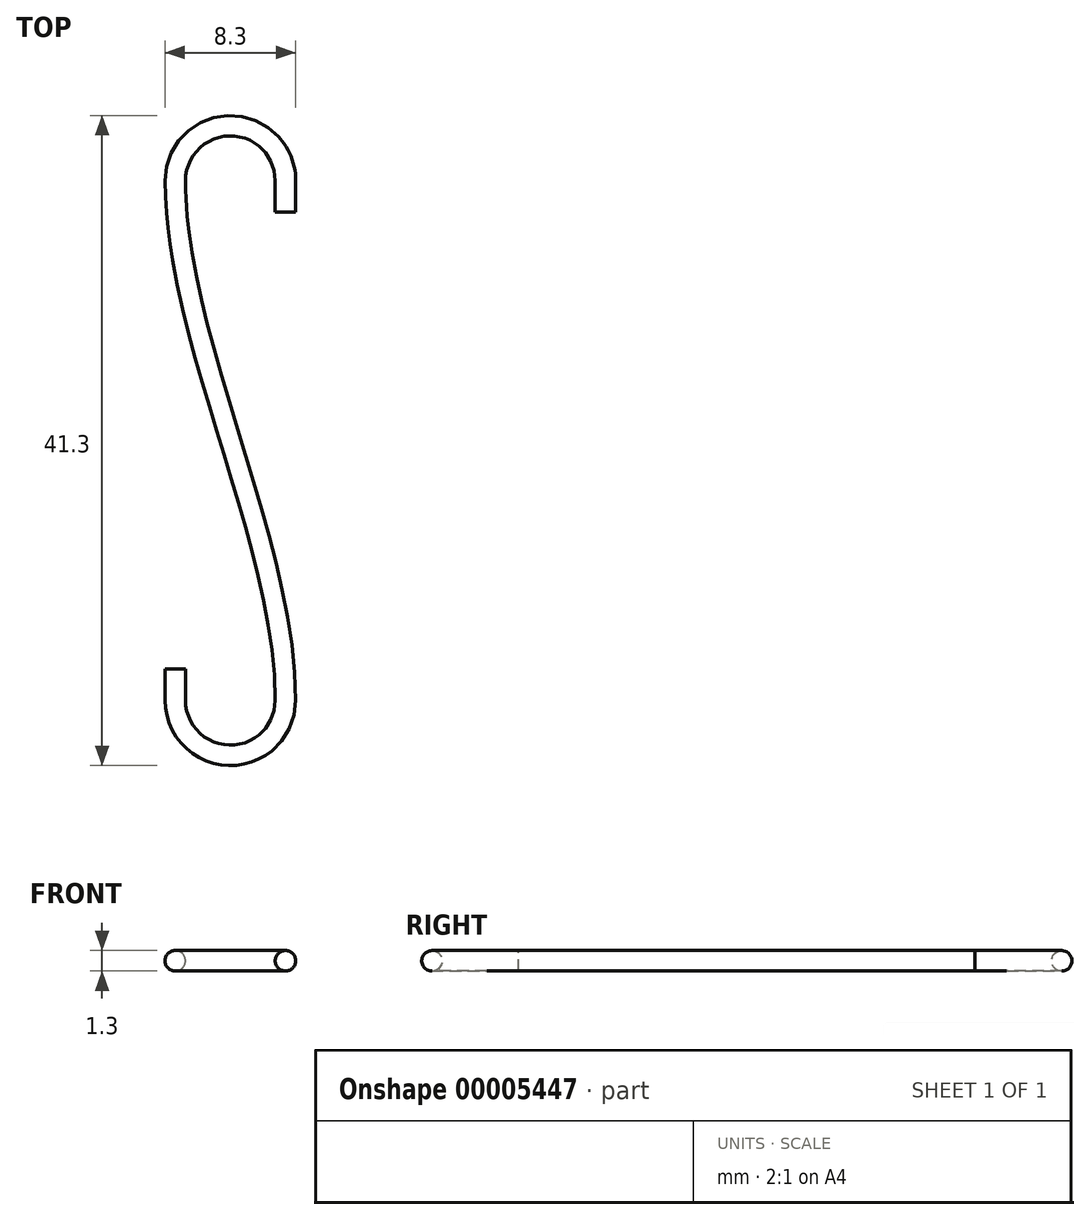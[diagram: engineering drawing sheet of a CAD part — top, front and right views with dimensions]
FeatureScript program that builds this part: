
annotation { "Feature Type Name" : "Feature", "Feature Type Description" : "" }
export const myFeature = defineFeature(function(context is Context, id is Id, definition is map)
    precondition{}
    {
        {
            var Q0;
            Q0=qCreatedBy(makeId("Top.planeOp"),FACE);
            var sketch = newSketch(context, id + "F0", { "sketchPlane" : qUnion([Q0])});
            skArc(sketch, "E0", {"start": v(3.5, 0) * mm, "mid": v(0, 3.5) * mm, "end": v(-3.5, 0) * mm});
            skArc(sketch, "E1", {"start": v(-3.5, -33) * mm, "mid": v(0, -36.5) * mm, "end": v(3.5, -33) * mm});
            skFitSpline(sketch, "E2", {"points": [v(-3.5, 0) * mm, v(3.5, -33) * mm], "startDerivative": vector(0, -30) * mm, "endDerivative": vector(0, -30) * mm});
            skLineSegment(sketch, "E3", {"start": v(-3.5, -33) * mm, "end": v(-3.5, -31) * mm});
            skLineSegment(sketch, "E4", {"start": v(3.5, 0) * mm, "end": v(3.5, -2) * mm});
            skLineSegment(sketch, "E5", {"start": v(0, 2.7) * mm, "end": v(0, -35.7) * mm, "construction": true});
            skLineSegment(sketch, "E6", {"start": v(0, 2.7) * mm, "end": v(0, 802.7) * mm, "construction": true});
            skSolve(sketch);
        }
        {
            var Q0;
            Q0=qCreatedBy(makeId("Front.planeOp"),FACE);
            var Q1;
            Q1=sQuery(id+"F0.wireOp",VERTEX,"E4.end");
            cPlane(context, id + "F1", {"entities" : qUnion([Q0, Q1]), "cplaneType" : CPlaneType.PLANE_POINT, "offset" : 25 * mm, "width" : 150 * mm, "height" : 150 * mm});
        }
        {
            var Q0;
            Q0=qCreatedBy(id+"F1.planeOp",FACE);
            var sketch = newSketch(context, id + "F2", { "sketchPlane" : qUnion([Q0])});
            skPoint(sketch, "E7.0", {"position": v(3.5, 0) * mm});
            skCircle(sketch, "E8", {"center": v(3.5, 0) * mm, "radius": 0.65 * mm});
            skSolve(sketch);
        }
        {
            var Q0;
            Q0=makeQuery(id+"F2.imprint","IMPRINT",FACE,{"disambiguationData":[TD([[makeQuery(id+"F2.imprint","IMPRINT",EDGE,{"derivedFrom":sQuery(id+"F2.wireOp",EDGE,"E8")}),1.0]])]});
            var Q1;
            Q1=sQuery(id+"F0.wireOp",EDGE,"E4");
            var Q2;
            Q2=sQuery(id+"F0.wireOp",EDGE,"E0");
            var Q3;
            Q3=sQuery(id+"F0.wireOp",EDGE,"E2");
            var Q4;
            Q4=sQuery(id+"F0.wireOp",EDGE,"E1");
            var Q5;
            Q5=sQuery(id+"F0.wireOp",EDGE,"E3");
            sweep(context, id + "F3", {"profiles" : qUnion([Q0]), "path" : qUnion([Q1, Q2, Q3, Q4, Q5])});
        }
    });
